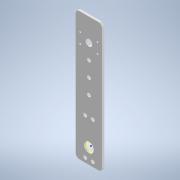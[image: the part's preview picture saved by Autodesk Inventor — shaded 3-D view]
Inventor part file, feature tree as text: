
AUTODESK INVENTOR PART (.ipt)
format: ipt  version: 2021 (Build 250183000, 183)  size: 138,240 bytes
history: native  units: mm
features: hole x4, sketch x3, extrude x2, other x1
ambient origin geometry x8: Origin, YZ Plane, XZ Plane, XY Plane, X Axis, Y Axis, Z Axis, Center Point
bodies: Body1 (feature_tree)
feature tree (10):
  other  "Sólido1"
  extrude  "Extrusión1"  Depth=10.0mm TaperAngle=0.0deg
  sketch  "Boceto2"  dims[d34=9.0mm d35=6.0mm d36=4.0mm d37=2.0mm d38=90.0deg d39=8.0mm d40=20.594885mm]
  hole  "Agujero1"  [1 undecoded]
  hole  "Agujero2"  [1 undecoded]
  hole  "Agujero3"  [1 undecoded]
  hole  "Agujero4"  [1 undecoded]
  extrude  "Extrusión2"  [1 undecoded]
  sketch  "Boceto1"  dims[d4=3.0mm d5=0.0mm]
  sketch  "Boceto3"  dims[d41=2.5mm d42=6.0mm d43=4.0mm d44=2.0mm d45=90.0deg d46=8.0mm d47=20.594885mm d48=5.0mm d49=6.0mm d50=4.0mm d51=2.0mm d52=90.0deg d53=8.0mm d54=20.594885mm d55=13.0mm d56=6.0mm d57=4.0mm d58=2.0mm d59=90.0deg d60=8.0mm d61=20.594885mm d66=10.0mm d67=0.0mm]
note: 5 required parameter values undecoded (feature->parameter linkage not recoverable at this tier; creation-order binding heuristic only, values carry confidence <= 0.55)
